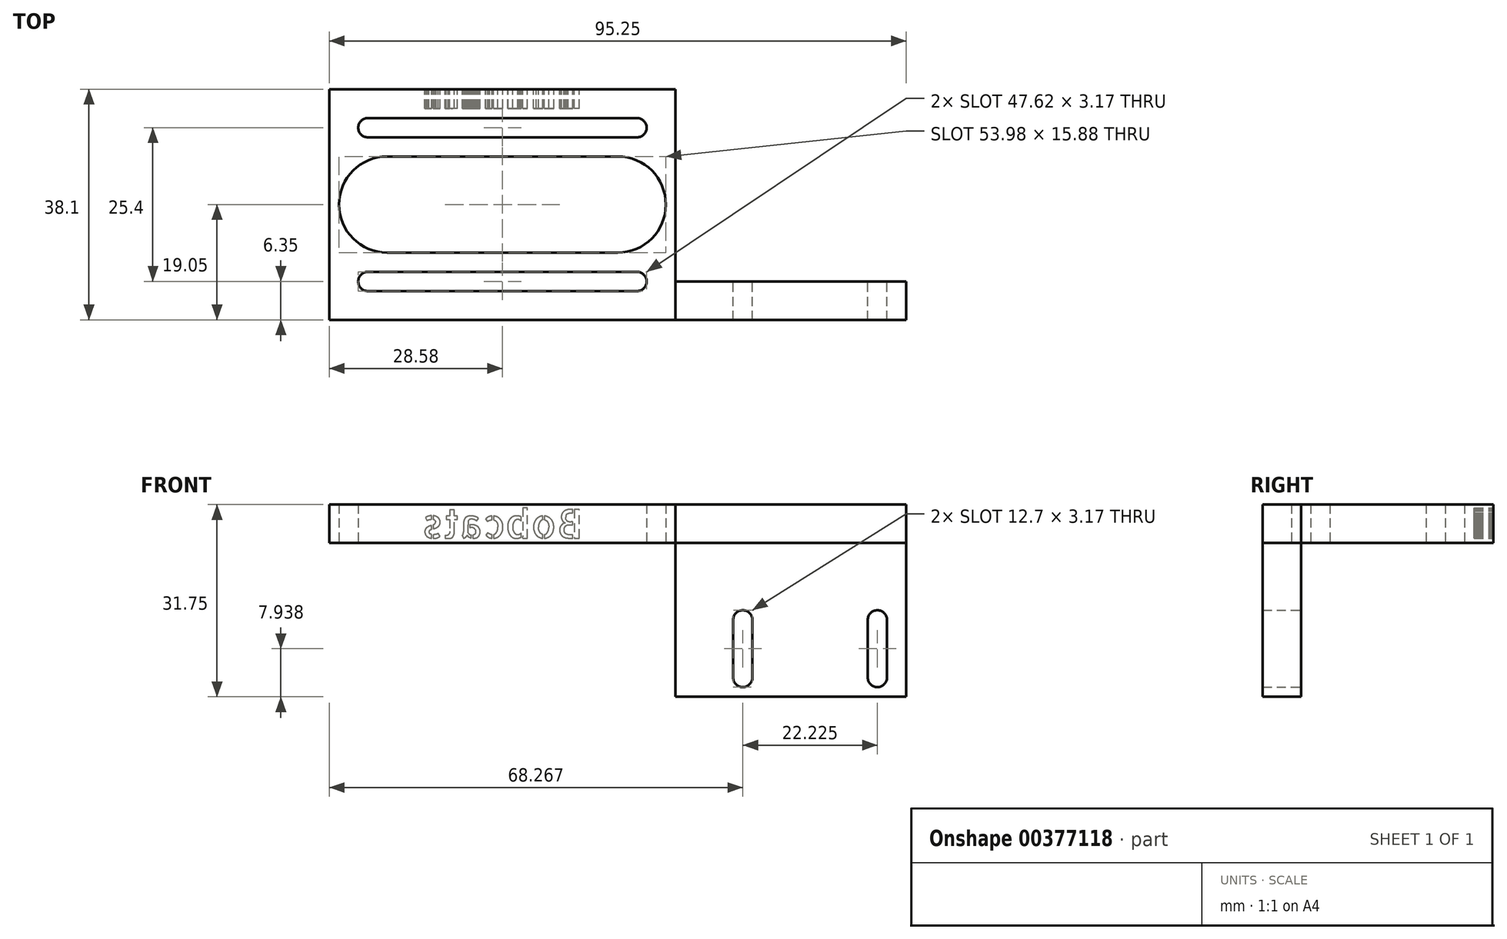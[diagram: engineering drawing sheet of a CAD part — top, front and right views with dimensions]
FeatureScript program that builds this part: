
annotation { "Feature Type Name" : "Feature", "Feature Type Description" : "" }
export const myFeature = defineFeature(function(context is Context, id is Id, definition is map)
    precondition{}
    {
        {
            var Q0;
            Q0=qCreatedBy(makeId("Top.planeOp"),FACE);
            var sketch = newSketch(context, id + "F0", { "sketchPlane" : qUnion([Q0])});
            skLineSegment(sketch, "E0.bottom", {"start": v(-28.58, 19.05) * mm, "end": v(28.58, 19.05) * mm});
            skLineSegment(sketch, "E0.top", {"start": v(-28.58, -19.05) * mm, "end": v(28.58, -19.05) * mm});
            skLineSegment(sketch, "E0.left", {"start": v(-28.58, 19.05) * mm, "end": v(-28.58, -19.05) * mm});
            skLineSegment(sketch, "E0.right", {"start": v(28.58, 19.05) * mm, "end": v(28.58, -19.05) * mm});
            skPoint(sketch, "E0.middle", {"position": v(0, 0) * mm});
            skLineSegment(sketch, "E1.bottom", {"start": v(28.58, -19.05) * mm, "end": v(66.68, -19.05) * mm});
            skLineSegment(sketch, "E1.top", {"start": v(28.58, -12.7) * mm, "end": v(66.68, -12.7) * mm});
            skLineSegment(sketch, "E1.left", {"start": v(28.58, -19.05) * mm, "end": v(28.58, -12.7) * mm});
            skLineSegment(sketch, "E1.right", {"start": v(66.68, -19.05) * mm, "end": v(66.68, -12.7) * mm});
            skLineSegment(sketch, "E2", {"start": v(28.58, 19.05) * mm, "end": v(66.68, -12.7) * mm});
            skPoint(sketch, "E3", {"position": v(0, -12.7) * mm});
            skPoint(sketch, "E4", {"position": v(0, 12.7) * mm});
            skLineSegment(sketch, "E5", {"start": v(-6.34, 12.7) * mm, "end": v(50.8, 12.7) * mm, "construction": true});
            skLineSegment(sketch, "E6", {"start": v(-22.94, -12.7) * mm, "end": v(21.76, -12.7) * mm, "construction": true});
            skLineSegment(sketch, "E7.bottom", {"start": v(22.23, 11.11) * mm, "end": v(-22.23, 11.11) * mm});
            skLineSegment(sketch, "E7.top", {"start": v(22.23, 14.29) * mm, "end": v(-22.23, 14.29) * mm});
            skLineSegment(sketch, "E7.left", {"start": v(22.23, 11.11) * mm, "end": v(22.23, 14.29) * mm});
            skLineSegment(sketch, "E7.right", {"start": v(-22.23, 11.11) * mm, "end": v(-22.23, 14.29) * mm});
            skPoint(sketch, "E7.cornerSnap0", {"position": v(22.23, 12.7) * mm});
            skLineSegment(sketch, "E8.bottom", {"start": v(22.23, -14.29) * mm, "end": v(-22.22, -14.29) * mm});
            skLineSegment(sketch, "E8.top", {"start": v(22.23, -11.11) * mm, "end": v(-22.22, -11.11) * mm});
            skLineSegment(sketch, "E8.left", {"start": v(22.23, -14.29) * mm, "end": v(22.23, -11.11) * mm});
            skLineSegment(sketch, "E8.right", {"start": v(-22.23, -14.29) * mm, "end": v(-22.23, -11.11) * mm});
            skCircle(sketch, "E9", {"center": v(-22.23, 12.7) * mm, "radius": 1.59 * mm});
            skCircle(sketch, "E10", {"center": v(22.23, 12.7) * mm, "radius": 1.59 * mm});
            skCircle(sketch, "E11", {"center": v(-22.23, -12.7) * mm, "radius": 1.59 * mm});
            skCircle(sketch, "E12", {"center": v(22.23, -12.7) * mm, "radius": 1.59 * mm});
            skLineSegment(sketch, "E13.bottom", {"start": v(-19.05, 7.94) * mm, "end": v(19.05, 7.94) * mm});
            skLineSegment(sketch, "E13.top", {"start": v(-19.05, -7.94) * mm, "end": v(19.05, -7.94) * mm});
            skLineSegment(sketch, "E13.left", {"start": v(-19.05, 7.94) * mm, "end": v(-19.05, -7.94) * mm});
            skLineSegment(sketch, "E13.right", {"start": v(19.05, 7.94) * mm, "end": v(19.05, -7.94) * mm});
            skCircle(sketch, "E14", {"center": v(-19.05, 0) * mm, "radius": 7.94 * mm});
            skCircle(sketch, "E15", {"center": v(19.05, 0) * mm, "radius": 7.94 * mm});
            skText(sketch, "E16", { "text": "C2\n", "fontName": "AllertaStencil-Regular.ttf"});
            skPoint(sketch, "E16.secondSnap0", {"position": v(47.63, -12.7) * mm});
            const initialGuessF0  = {"E16": [0.03604, -0.0066, 1, 0, 0.00665]};
            skSetInitialGuess(sketch, initialGuessF0);
            skSolve(sketch);
        }
        {
            var Q0;
            Q0=makeQuery(id+"F0.imprint","IMPRINT",FACE,{"disambiguationData":[TD([[makeQuery(id+"F0.imprint","IMPRINT",EDGE,{"derivedFrom":sQuery(id+"F0.wireOp",EDGE,"E0.bottom")}),-1.0]])]});
            extrude(context, id + "F1", {"entities" : qUnion([Q0]), "depth" : 6.35 * mm, "offsetDistance" : 25.4 * mm});
        }
        {
            var Q0;
            Q0=makeQuery(id+"F0.imprint","IMPRINT",FACE,{"disambiguationData":[TD([[makeQuery(id+"F0.imprint","IMPRINT",EDGE,{"derivedFrom":sQuery(id+"F0.wireOp",EDGE,"E1.bottom")}),1.0]])]});
            extrude(context, id + "F2", {"entities" : qUnion([Q0]), "operationType" : NewBodyOperationType.ADD, "oppositeDirection" : true, "depth" : 25.4 * mm, "offsetDistance" : 25.4 * mm});
        }
        {
            var Q0;
            Q0=makeQuery(id+"F0.imprint","IMPRINT",FACE,{"disambiguationData":[TD([[makeQuery(id+"F0.imprint","IMPRINT",EDGE,{"derivedFrom":sQuery(id+"F0.wireOp",EDGE,"E0.right")}),1.0]])]});
            extrude(context, id + "F3", {"entities" : qUnion([Q0]), "operationType" : NewBodyOperationType.ADD, "depth" : 6.35 * mm});
        }
        {
            var Q0;
            Q0=makeQuery(id+"F1.opExtrude","SWEPT_FACE",FACE,{"disambiguationData":[OSD([sQuery(id+"F0.wireOp",EDGE,"E0.bottom")])]});
            var sketch = newSketch(context, id + "F4", { "sketchPlane" : qUnion([Q0])});
            skText(sketch, "E17", { "text": "Bobcats", "fontName": "AllertaStencil-Regular.ttf"});
            const initialGuessF4  = {"E17": [-0.01328, 0.0008, 1, 0, 0.00476]};
            skSetInitialGuess(sketch, initialGuessF4);
            skSolve(sketch);
        }
        {
            var Q0;
            Q0 = qSketchRegion(id + "F4", true);
            extrude(context, id + "F5", {"entities" : qUnion([Q0]), "operationType" : NewBodyOperationType.REMOVE, "oppositeDirection" : true, "depth" : 3.17 * mm});
        }
        {
            var Q0;
            Q0=makeQuery(id+"F2.opExtrude","SWEPT_FACE",FACE,{"disambiguationData":[OSD([sQuery(id+"F0.wireOp",EDGE,"E1.top")])]});
            var sketch = newSketch(context, id + "F6", { "sketchPlane" : qUnion([Q0])});
            skLineSegment(sketch, "E18.bottom", {"start": v(-63.5, -12.7) * mm, "end": v(-60.33, -12.7) * mm});
            skLineSegment(sketch, "E18.top", {"start": v(-63.5, -22.23) * mm, "end": v(-60.33, -22.23) * mm});
            skLineSegment(sketch, "E18.left", {"start": v(-63.5, -12.7) * mm, "end": v(-63.5, -22.22) * mm});
            skLineSegment(sketch, "E18.right", {"start": v(-60.33, -12.7) * mm, "end": v(-60.33, -22.23) * mm});
            skCircle(sketch, "E19", {"center": v(-61.91, -12.7) * mm, "radius": 1.59 * mm});
            skCircle(sketch, "E20", {"center": v(-61.91, -22.23) * mm, "radius": 1.59 * mm});
            skLineSegment(sketch, "E21.bottom", {"start": v(-41.28, -12.7) * mm, "end": v(-38.1, -12.7) * mm});
            skLineSegment(sketch, "E21.top", {"start": v(-41.28, -22.22) * mm, "end": v(-38.1, -22.22) * mm});
            skLineSegment(sketch, "E21.left", {"start": v(-41.28, -12.7) * mm, "end": v(-41.28, -22.22) * mm});
            skLineSegment(sketch, "E21.right", {"start": v(-38.1, -12.7) * mm, "end": v(-38.1, -22.22) * mm});
            skCircle(sketch, "E22", {"center": v(-39.69, -12.7) * mm, "radius": 1.59 * mm});
            skCircle(sketch, "E23", {"center": v(-39.69, -22.22) * mm, "radius": 1.59 * mm});
            skSolve(sketch);
        }
        {
            var Q0;
            {var subQ0=sQuery(id+"F6.wireOp",EDGE,"E18.bottom");Q0=makeQuery(id+"F6.imprint","IMPRINT",FACE,{"disambiguationData":[TD([[makeQuery(id+"F6.imprint","IMPRINT",EDGE,{"derivedFrom":subQ0}),1.0]])]});}
            var Q1;
            {var subQ0=sQuery(id+"F6.wireOp",EDGE,"E18.bottom");Q1=makeQuery(id+"F6.imprint","IMPRINT",FACE,{"disambiguationData":[TD([[makeQuery(id+"F6.imprint","IMPRINT",EDGE,{"derivedFrom":subQ0}),-1.0]])]});}
            var Q2;
            {var subQ0=sQuery(id+"F6.wireOp",EDGE,"E18.left");Q2=makeQuery(id+"F6.imprint","IMPRINT",FACE,{"disambiguationData":[TD([[makeQuery(id+"F6.imprint","IMPRINT",EDGE,{"derivedFrom":subQ0}),1.0]])]});}
            var Q3;
            {var subQ0=sQuery(id+"F6.wireOp",EDGE,"E18.top");Q3=makeQuery(id+"F6.imprint","IMPRINT",FACE,{"disambiguationData":[TD([[makeQuery(id+"F6.imprint","IMPRINT",EDGE,{"derivedFrom":subQ0}),1.0]])]});}
            var Q4;
            {var subQ0=sQuery(id+"F6.wireOp",EDGE,"E18.top");Q4=makeQuery(id+"F6.imprint","IMPRINT",FACE,{"disambiguationData":[TD([[makeQuery(id+"F6.imprint","IMPRINT",EDGE,{"derivedFrom":subQ0}),-1.0]])]});}
            var Q5;
            {var subQ0=sQuery(id+"F6.wireOp",EDGE,"Fqk9zLaz-Kd5e-vRgL-821y-cBg3t54pUeUE.left");Q5=makeQuery(id+"F6.imprint","IMPRINT",FACE,{"disambiguationData":[TD([[makeQuery(id+"F6.imprint","IMPRINT",EDGE,{"derivedFrom":subQ0}),-1.0]])]});}
            var Q6;
            {var subQ0=sQuery(id+"F6.wireOp",EDGE,"Fqk9zLaz-Kd5e-vRgL-821y-cBg3t54pUeUE.left");Q6=makeQuery(id+"F6.imprint","IMPRINT",FACE,{"disambiguationData":[TD([[makeQuery(id+"F6.imprint","IMPRINT",EDGE,{"derivedFrom":subQ0}),1.0]])]});}
            var Q7;
            {var subQ0=sQuery(id+"F6.wireOp",EDGE,"Fqk9zLaz-Kd5e-vRgL-821y-cBg3t54pUeUE.bottom");Q7=makeQuery(id+"F6.imprint","IMPRINT",FACE,{"disambiguationData":[TD([[makeQuery(id+"F6.imprint","IMPRINT",EDGE,{"derivedFrom":subQ0}),-1.0]])]});}
            var Q8;
            {var subQ0=sQuery(id+"F6.wireOp",EDGE,"Fqk9zLaz-Kd5e-vRgL-821y-cBg3t54pUeUE.right");Q8=makeQuery(id+"F6.imprint","IMPRINT",FACE,{"disambiguationData":[TD([[makeQuery(id+"F6.imprint","IMPRINT",EDGE,{"derivedFrom":subQ0}),-1.0]])]});}
            var Q9;
            {var subQ0=sQuery(id+"F6.wireOp",EDGE,"Fqk9zLaz-Kd5e-vRgL-821y-cBg3t54pUeUE.right");Q9=makeQuery(id+"F6.imprint","IMPRINT",FACE,{"disambiguationData":[TD([[makeQuery(id+"F6.imprint","IMPRINT",EDGE,{"derivedFrom":subQ0}),1.0]])]});}
            var Q10;
            {var subQ0=sQuery(id+"F6.wireOp",EDGE,"E21.bottom");Q10=makeQuery(id+"F6.imprint","IMPRINT",FACE,{"disambiguationData":[TD([[makeQuery(id+"F6.imprint","IMPRINT",EDGE,{"derivedFrom":subQ0}),1.0]])]});}
            var Q11;
            {var subQ0=sQuery(id+"F6.wireOp",EDGE,"E21.bottom");Q11=makeQuery(id+"F6.imprint","IMPRINT",FACE,{"disambiguationData":[TD([[makeQuery(id+"F6.imprint","IMPRINT",EDGE,{"derivedFrom":subQ0}),-1.0]])]});}
            var Q12;
            {var subQ0=sQuery(id+"F6.wireOp",EDGE,"E21.left");Q12=makeQuery(id+"F6.imprint","IMPRINT",FACE,{"disambiguationData":[TD([[makeQuery(id+"F6.imprint","IMPRINT",EDGE,{"derivedFrom":subQ0}),1.0]])]});}
            var Q13;
            {var subQ0=sQuery(id+"F6.wireOp",EDGE,"E21.top");Q13=makeQuery(id+"F6.imprint","IMPRINT",FACE,{"disambiguationData":[TD([[makeQuery(id+"F6.imprint","IMPRINT",EDGE,{"derivedFrom":subQ0}),1.0]])]});}
            var Q14;
            {var subQ0=sQuery(id+"F6.wireOp",EDGE,"E21.top");Q14=makeQuery(id+"F6.imprint","IMPRINT",FACE,{"disambiguationData":[TD([[makeQuery(id+"F6.imprint","IMPRINT",EDGE,{"derivedFrom":subQ0}),-1.0]])]});}
            extrude(context, id + "F7", {"entities" : qUnion([Q0, Q1, Q2, Q3, Q4, Q5, Q6, Q7, Q8, Q9, Q10, Q11, Q12, Q13, Q14]), "operationType" : NewBodyOperationType.REMOVE, "oppositeDirection" : true, "depth" : 25.4 * mm, "offsetDistance" : 25.4 * mm});
        }
        {
            var Q0;
            Q0=makeQuery(id+"F0.imprint","IMPRINT",FACE,{"disambiguationData":[TD([[makeQuery(id+"F0.imprint","IMPRINT",EDGE,{"derivedFrom":sQuery(id+"F0.wireOp",EDGE,"E1.bottom")}),1.0]])]});
            extrude(context, id + "F8", {"entities" : qUnion([Q0]), "depth" : 6.35 * mm, "offsetDistance" : 25.4 * mm});
        }
    });
